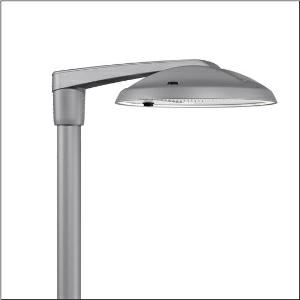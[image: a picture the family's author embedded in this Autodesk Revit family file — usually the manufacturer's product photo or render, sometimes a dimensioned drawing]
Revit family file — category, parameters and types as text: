
# Revit family: dl_r__50_iq_mini___st1_0a_5xa248d31y08ne_98a7
name_source: partatom
category: Lighting Fixtures
units: mm (PartAtom-declared; Revit-internal decimal feet)

## family parameters
Cut with Voids When Loaded = No
Host = Face
Light Source = No
Part Type = Normal
Room Calculation Point = No
Round Connector Dimension = Use Diameter
Shared = No

## types (1)
- --- (1 x LED, 17900 lm, 110.1 W, 3000K)
    Apparent Load = 110 VA
    CIE Flux Codes = 37 72 97 100 100
    Color Rendering = 70
    Color Temperature = 3000K
    Default Elevation = 1800 mm
    Description = DL® 50 iQ mini, mast luminaire, primary light control with lens, of PMMA, primary optical cover: cover, of toughened safety glass, transparent, light distribution: ST1.0a, light emission: direct distribution, primary light characteristic: asymmetric, installation type: post-top, side-entry, LED, High Power LED, rated luminous flux: 17.900lm, luminous efficacy: 163lm/W, light colour: 730, colour temperature: 3000K, control: optimised constant luminous flux control (CLO 2.0), Desk-Remote (wireless, voltage-free reading and setting of iQ features in the workshop via application-optimized NFC function/RFID function), Light-Fading, Smart-Wire, Night-Set, Lumen-Switch, Temp-Guard, Auto-Match, Street-Remote, pre-setting: logarithmic dimming characteristic, mains connection: 230..240V, AC, 50/60Hz, connection cable pre-assembled, cable length: 10,5m, start of lifetime: 110W, end of service life: 116W, reduction: 50W, luminaire housing, of diecast aluminium, powder-coated, Siteco® metallic grey (DB 702S), inclination adjustable: 0°, 5°, 10° (post-top) | 0°, -5°, -10°, -15° (side-entry), please order mast post-top element or mast side-entry element separately, diameter: 500mm, height: 115mm, post-top: for spigot size d x l = 76 x 100mm; with reducer (optional accessory) 60 x 100mm | side-entry: for spigot size d x l = 60 x 100mm; with reducer (optional accessory) 42 x 100mm, Smart Interface below and above, protection rating (complete): IP66, insulation class (complete): insulation class II (safety insulation), certification: CE, ENEC, ENEC+, VDE, impact resistance: IK08, permissible operating ambient temperature for outdoor applications: -25..+40°C, standard-compliant lighting for roads and squares, packaging unit: 1 piece

Light Distribution: ST1.0a
    Height = 115 mm
    Lamp = 1 x LED
    Lamp Light Flux = 17900 lm
    Lamp Power = 110.1 W
    Lamp count = 1
    Length = 500 mm
    Luminous efficacy = 163 lm/W
    Manufacturer = Siteco
    ModVariant = No
    Model = 5XA248D31Y08NE
    Number of Poles = 1
    OnlyDefault = Yes
    Power Factor = 1
    Product Name = DL® 50 iQ mini | ST1.0a
    Product group = mast luminaire | pylon top
    ProductGroupID = 6100
    Protection Class = Protection class II
    Protection Degree = IP 66
    RLX_Detail_Level = 1
    RLX_Emergency_Light_Flux = 0 lm
    RLX_Emergency_Type = 0
    RLX_Emergency_Type_DB = No
    RlxData = <blob elided: 106761 chars, md5=61a1a67e>
    Socket = socket
    Standby Power = 0 W
    System Light Flux = 17900 lm
    System Power = 110 W
    Type Comments = factory setting: luminous flux: 100 % | dim-lin: 254 | 601 mA
    Type Image = l_1251786.jpg
    URL = http://relux.com
    VarID = @adj_033319
    Voltage = 0 V
    Weight = 0.00 kg
    Width = 0 mm  [stored 0 ft]

note: [stored X ft] marks values corroborated as IEEE doubles in the binary element streams (Revit-internal decimal feet)

## geometry (parser evidence)
native form markers: Blend x4, Sweep x10
no freeform markers — native parametric forms only
